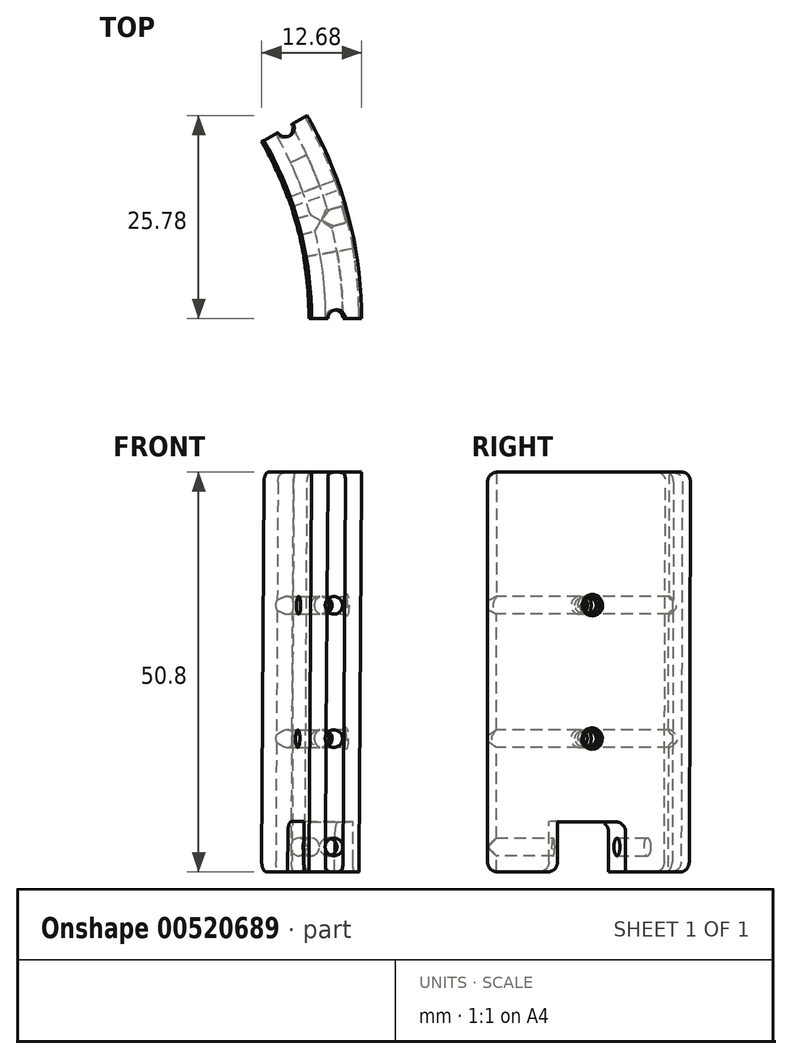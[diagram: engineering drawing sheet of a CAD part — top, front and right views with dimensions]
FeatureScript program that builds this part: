
annotation { "Feature Type Name" : "Feature", "Feature Type Description" : "" }
export const myFeature = defineFeature(function(context is Context, id is Id, definition is map)
    precondition{}
    {
        {
            var Q0;
            Q0=qCreatedBy(makeId("Front.planeOp"),FACE);
            var sketch = newSketch(context, id + "F0", { "sketchPlane" : qUnion([Q0])});
            skLineSegment(sketch, "E0", {"start": v(0, 0) * mm, "end": v(0, 50.8) * mm});
            skLineSegment(sketch, "E1", {"start": v(0, 50.8) * mm, "end": v(51.56, 50.8) * mm});
            skLineSegment(sketch, "E2", {"start": v(0, 0) * mm, "end": v(51.23, 0) * mm});
            skLineSegment(sketch, "E3", {"start": v(51.23, 0) * mm, "end": v(51.56, 50.8) * mm});
            skSolve(sketch);
        }
        {
            var Q0;
            Q0=makeQuery(id+"F0.imprint","IMPRINT",FACE,{"disambiguationData":[TD([[makeQuery(id+"F0.imprint","IMPRINT",EDGE,{"derivedFrom":sQuery(id+"F0.wireOp",EDGE,"E0")}),-1.0]])]});
            var Q1;
            Q1=sQuery(id+"F0.wireOp",EDGE,"E0");
            revolve(context, id + "F1", {"entities" : qUnion([Q0]), "axis" : qUnion([Q1]), "revolveType" : RevolveType.ONE_DIRECTION, "angle" : 30 * degree});
        }
        {
            var Q0;
            Q0=makeQuery(id+"F1.opRevolve","CAP_FACE",FACE,{"disambiguationData":[OSD([sQuery(id+"F0.wireOp",EDGE,"E0"),sQuery(id+"F0.wireOp",EDGE,"E1"),sQuery(id+"F0.wireOp",EDGE,"E2"),sQuery(id+"F0.wireOp",EDGE,"E3")])],"isStart":true});
            var sketch = newSketch(context, id + "F2", { "sketchPlane" : qUnion([Q0])});
            skLineSegment(sketch, "E4", {"start": v(0, 50.8) * mm, "end": v(0, 0) * mm});
            skLineSegment(sketch, "E5", {"start": v(0, 0) * mm, "end": v(44.88, 0) * mm});
            skLineSegment(sketch, "E6", {"start": v(0, 50.8) * mm, "end": v(45.21, 50.8) * mm});
            skLineSegment(sketch, "E7", {"start": v(45.21, 50.8) * mm, "end": v(44.88, 0) * mm});
            skSolve(sketch);
        }
        {
            var Q0;
            Q0=qSketchRegion(id+"F2",true);
            var Q1;
            Q1=sQuery(id+"F2.wireOp",EDGE,"E4");
            revolve(context, id + "F3", {"operationType" : NewBodyOperationType.REMOVE, "entities" : qUnion([Q0]), "axis" : qUnion([Q1]), "revolveType" : RevolveType.FULL, "oppositeDirection" : true});
        }
        {
            var Q0;
            Q0=makeQuery(id+"F1.opRevolve","CAP_FACE",FACE,{"disambiguationData":[OSD([sQuery(id+"F0.wireOp",EDGE,"E0"),sQuery(id+"F0.wireOp",EDGE,"E1"),sQuery(id+"F0.wireOp",EDGE,"E2"),sQuery(id+"F0.wireOp",EDGE,"E3")])],"isStart":true});
            var sketch = newSketch(context, id + "F4", { "sketchPlane" : qUnion([Q0])});
            skLineSegment(sketch, "E8", {"start": v(0, 0) * mm, "end": v(51.23, 0) * mm, "construction": true});
            skLineSegment(sketch, "E9", {"start": v(51.23, 0) * mm, "end": v(51.27, 6.35) * mm});
            skLineSegment(sketch, "E10", {"start": v(51.27, 6.35) * mm, "end": v(44.92, 6.4) * mm});
            skLineSegment(sketch, "E11", {"start": v(44.92, 6.4) * mm, "end": v(44.88, 0) * mm});
            skLineSegment(sketch, "E12", {"start": v(44.88, 0) * mm, "end": v(51.23, 0) * mm});
            skLineSegment(sketch, "E13", {"start": v(0, -1.63) * mm, "end": v(0, 22.61) * mm, "construction": true});
            skSolve(sketch);
        }
        {
            var Q0;
            Q0=qSketchRegion(id+"F4",true);
            var Q1;
            Q1=sQuery(id+"F4.wireOp",EDGE,"E13");
            revolve(context, id + "F5", {"operationType" : NewBodyOperationType.REMOVE, "entities" : qUnion([Q0]), "axis" : qUnion([Q1]), "revolveType" : RevolveType.ONE_DIRECTION, "angle" : 20 * degree});
        }
        {
            var Q0;
            Q0=qSketchRegion(id+"F4",true);
            var Q1;
            Q1=sQuery(id+"F4.wireOp",EDGE,"E13");
            revolve(context, id + "F6", {"operationType" : NewBodyOperationType.ADD, "entities" : qUnion([Q0]), "axis" : qUnion([Q1]), "revolveType" : RevolveType.ONE_DIRECTION, "angle" : 10 * degree});
        }
        {
            var Q0;
            Q0=makeQuery(id+"F6.boolean.opBoolean","MERGE",FACE,{"derivedFrom":[makeQuery(id+"F1.opRevolve","CAP_FACE",FACE,{"disambiguationData":[OSD([sQuery(id+"F0.wireOp",EDGE,"E0"),sQuery(id+"F0.wireOp",EDGE,"E1"),sQuery(id+"F0.wireOp",EDGE,"E2"),sQuery(id+"F0.wireOp",EDGE,"E3")])],"isStart":true}),makeQuery(id+"F6.opRevolve","CAP_FACE",FACE,{"disambiguationData":[OSD([sQuery(id+"F4.wireOp",EDGE,"E9"),sQuery(id+"F4.wireOp",EDGE,"E10"),sQuery(id+"F4.wireOp",EDGE,"E11"),sQuery(id+"F4.wireOp",EDGE,"E12")])],"isStart":true})]});
            var sketch = newSketch(context, id + "F7", { "sketchPlane" : qUnion([Q0])});
            skLineSegment(sketch, "E14", {"start": v(0, 0) * mm, "end": v(0, 25.16) * mm, "construction": true});
            skLineSegment(sketch, "E15", {"start": v(45.21, 50.8) * mm, "end": v(48.39, 50.8) * mm, "construction": true});
            skLineSegment(sketch, "E16", {"start": v(44.88, 0) * mm, "end": v(48.06, 0) * mm, "construction": true});
            skLineSegment(sketch, "E17", {"start": v(48.06, 0) * mm, "end": v(48.08, 4.3) * mm, "construction": true});
            skPoint(sketch, "E18", {"position": v(48.08, 3.17) * mm});
            skCircle(sketch, "E19", {"center": v(48.08, 3.17) * mm, "radius": 1.12 * mm, "construction": true});
            skLineSegment(sketch, "E20", {"start": v(0, 0) * mm, "end": v(48.06, 0) * mm, "construction": true});
            skLineSegment(sketch, "E21", {"start": v(48.06, 0) * mm, "end": v(48.06, 16.93) * mm, "construction": true});
            skLineSegment(sketch, "E22", {"start": v(48.06, 16.93) * mm, "end": v(48.06, 33.87) * mm, "construction": true});
            skCircle(sketch, "E23", {"center": v(48.06, 33.87) * mm, "radius": 1.12 * mm});
            skCircle(sketch, "E24", {"center": v(48.06, 16.93) * mm, "radius": 1.12 * mm});
            skSolve(sketch);
        }
        {
            var Q0;
            Q0=qSketchRegion(id+"F7",true);
            var Q1;
            Q1=sQuery(id+"F7.wireOp",EDGE,"E14");
            revolve(context, id + "F8", {"operationType" : NewBodyOperationType.REMOVE, "entities" : qUnion([Q0]), "axis" : qUnion([Q1]), "revolveType" : RevolveType.FULL, "oppositeDirection" : true});
        }
        {
            var Q0;
            Q0=makeQuery(id+"F6.opRevolve","SWEPT_FACE",FACE,{"disambiguationData":[OSD([sQuery(id+"F4.wireOp",EDGE,"E12")])]});
            var sketch = newSketch(context, id + "F9", { "sketchPlane" : qUnion([Q0])});
            skLineSegment(sketch, "E25", {"start": v(51.23, 0) * mm, "end": v(48.06, 0) * mm, "construction": true});
            skCircle(sketch, "E26", {"center": v(48.06, 0) * mm, "radius": 1.11 * mm});
            skSolve(sketch);
        }
        {
            var Q0;
            Q0=makeQuery(id+"F1.opRevolve","SWEPT_FACE",FACE,{"disambiguationData":[OSD([sQuery(id+"F0.wireOp",EDGE,"E1")])]});
            var sketch = newSketch(context, id + "F10", { "sketchPlane" : qUnion([Q0])});
            skLineSegment(sketch, "E27", {"start": v(51.56, 0) * mm, "end": v(48.39, 0) * mm, "construction": true});
            skCircle(sketch, "E28", {"center": v(48.39, 0) * mm, "radius": 1.11 * mm});
            skSolve(sketch);
        }
        {
            var Q0;
            Q0=makeQuery(id+"F1.opRevolve","SWEPT_FACE",FACE,{"disambiguationData":[OSD([sQuery(id+"F0.wireOp",EDGE,"E2")])]});
            var sketch = newSketch(context, id + "F11", { "sketchPlane" : qUnion([Q0])});
            skLineSegment(sketch, "E29", {"start": v(44.37, -25.62) * mm, "end": v(41.62, -24.03) * mm, "construction": true});
            skCircle(sketch, "E30", {"center": v(41.62, -24.03) * mm, "radius": 1.11 * mm});
            skSolve(sketch);
        }
        {
            var Q0;
            Q0=makeQuery(id+"F1.opRevolve","SWEPT_FACE",FACE,{"disambiguationData":[OSD([sQuery(id+"F0.wireOp",EDGE,"E1")])]});
            var sketch = newSketch(context, id + "F12", { "sketchPlane" : qUnion([Q0])});
            skLineSegment(sketch, "E31", {"start": v(44.65, 25.78) * mm, "end": v(41.9, 24.2) * mm, "construction": true});
            skCircle(sketch, "E32", {"center": v(41.9, 24.2) * mm, "radius": 1.11 * mm});
            skSolve(sketch);
        }
        {
            var Q0;
            Q0=makeQuery(id+"F5.boolean.opBoolean","COPY",EDGE,{"derivedFrom":makeQuery(id+"F5.opRevolve","CAP_EDGE",EDGE,{"disambiguationData":[OSD([sQuery(id+"F4.wireOp",EDGE,"E10")])],"isStart":false})});
            var Q1;
            Q1=makeQuery(id+"F5.boolean.opBoolean","COPY",EDGE,{"derivedFrom":makeQuery(id+"F5.opRevolve","CAP_EDGE",EDGE,{"disambiguationData":[OSD([sQuery(id+"F4.wireOp",EDGE,"E12")])],"isStart":false})});
            var Q2;
            Q2=makeQuery(id+"F6.opRevolve","CAP_EDGE",EDGE,{"disambiguationData":[OSD([sQuery(id+"F4.wireOp",EDGE,"E12")])],"isStart":false});
            var Q3;
            Q3=makeQuery(id+"F6.opRevolve","CAP_EDGE",EDGE,{"disambiguationData":[OSD([sQuery(id+"F4.wireOp",EDGE,"E10")])],"isStart":false});
            var Q4;
            Q4=makeQuery(id+"F1.opRevolve","CAP_EDGE",EDGE,{"disambiguationData":[OSD([sQuery(id+"F0.wireOp",EDGE,"E2")])],"isStart":false});
            var Q5;
            Q5=makeQuery(id+"F6.opRevolve","CAP_EDGE",EDGE,{"disambiguationData":[OSD([sQuery(id+"F4.wireOp",EDGE,"E12")])],"isStart":true});
            var Q6;
            Q6=makeQuery(id+"F1.opRevolve","CAP_EDGE",EDGE,{"disambiguationData":[OSD([sQuery(id+"F0.wireOp",EDGE,"E1")])],"isStart":true});
            var Q7;
            Q7=makeQuery(id+"F1.opRevolve","CAP_EDGE",EDGE,{"disambiguationData":[OSD([sQuery(id+"F0.wireOp",EDGE,"E1")])],"isStart":false});
            fillet(context, id + "F13", {"entities" : qUnion([Q0, Q1, Q2, Q3, Q4, Q5, Q6, Q7]), "radius" : 1.27 * mm, "tangentPropagation" : true, "allowEdgeOverflow" : false});
        }
        {
            var Q0;
            Q0=qCreatedBy(makeId("Front.planeOp"),FACE);
            var sketch = newSketch(context, id + "F14", { "sketchPlane" : qUnion([Q0])});
            skLineSegment(sketch, "E33", {"start": v(0, 0) * mm, "end": v(48.06, 0) * mm, "construction": true});
            skLineSegment(sketch, "E34", {"start": v(48.06, 0) * mm, "end": v(48.06, 3.18) * mm, "construction": true});
            skCircle(sketch, "E35", {"center": v(48.06, 3.18) * mm, "radius": 1.12 * mm});
            skSolve(sketch);
        }
        {
            var Q0;
            Q0=qSketchRegion(id+"F14",true);
            var Q1;
            Q1=sQuery(id+"F7.wireOp",EDGE,"E14");
            revolve(context, id + "F15", {"operationType" : NewBodyOperationType.REMOVE, "entities" : qUnion([Q0]), "axis" : qUnion([Q1]), "revolveType" : RevolveType.ONE_DIRECTION, "angle" : 25 * degree});
        }
        {
            var Q1;
            {var subQ0=sQuery(id+"F10.wireOp",EDGE,"E28");var subQ1=makeQuery(id+"F1.opRevolve","CAP_EDGE",EDGE,{"disambiguationData":[OSD([sQuery(id+"F0.wireOp",EDGE,"E1")])],"isStart":true});var subQ2=makeQuery(id+"F10.imprint","INTERSECT",VERTEX,{"disambiguationData":[OD(0.0)],"derivedFrom":[subQ1,subQ0]});Q1=makeQuery(id+"F10.imprint","IMPRINT",FACE,{"disambiguationData":[TD([[makeQuery(id+"F10.imprint","IMPRINT",EDGE,{"disambiguationData":[TD([[subQ2,-1.0]])],"derivedFrom":subQ0}),1.0]])]});}
            var Q2;
            {var subQ0=sQuery(id+"F9.wireOp",EDGE,"E26");var subQ1=makeQuery(id+"F6.opRevolve","CAP_EDGE",EDGE,{"disambiguationData":[OSD([sQuery(id+"F4.wireOp",EDGE,"E12")])],"isStart":true});var subQ2=makeQuery(id+"F9.imprint","INTERSECT",VERTEX,{"disambiguationData":[OD(0.0)],"derivedFrom":[subQ1,subQ0]});Q2=makeQuery(id+"F9.imprint","IMPRINT",FACE,{"disambiguationData":[TD([[makeQuery(id+"F9.imprint","IMPRINT",EDGE,{"disambiguationData":[TD([[subQ2,1.0]])],"derivedFrom":subQ0}),1.0]])]});}
            loft(context, id + "F16", {"operationType" : NewBodyOperationType.REMOVE, "sheetProfilesArray" : [{ "sheetProfileEntities" : qUnion([Q1]) }, { "sheetProfileEntities" : qUnion([Q2]) }]});
        }
        {
            var Q1;
            {var subQ0=sQuery(id+"F12.wireOp",EDGE,"E32");var subQ1=makeQuery(id+"F1.opRevolve","CAP_EDGE",EDGE,{"disambiguationData":[OSD([sQuery(id+"F0.wireOp",EDGE,"E1")])],"isStart":false});var subQ2=makeQuery(id+"F12.imprint","INTERSECT",VERTEX,{"disambiguationData":[OD(0.0)],"derivedFrom":[subQ1,subQ0]});Q1=makeQuery(id+"F12.imprint","IMPRINT",FACE,{"disambiguationData":[TD([[makeQuery(id+"F12.imprint","IMPRINT",EDGE,{"disambiguationData":[TD([[subQ2,1.0]])],"derivedFrom":subQ0}),1.0]])]});}
            var Q2;
            {var subQ0=sQuery(id+"F11.wireOp",EDGE,"E30");var subQ1=makeQuery(id+"F1.opRevolve","CAP_EDGE",EDGE,{"disambiguationData":[OSD([sQuery(id+"F0.wireOp",EDGE,"E2")])],"isStart":false});var subQ2=makeQuery(id+"F11.imprint","INTERSECT",VERTEX,{"disambiguationData":[OD(0.0)],"derivedFrom":[subQ1,subQ0]});Q2=makeQuery(id+"F11.imprint","IMPRINT",FACE,{"disambiguationData":[TD([[makeQuery(id+"F11.imprint","IMPRINT",EDGE,{"disambiguationData":[TD([[subQ2,-1.0]])],"derivedFrom":subQ0}),1.0]])]});}
            loft(context, id + "F17", {"operationType" : NewBodyOperationType.REMOVE, "sheetProfilesArray" : [{ "sheetProfileEntities" : qUnion([Q1]) }, { "sheetProfileEntities" : qUnion([Q2]) }]});
        }
        {
            var Q0;
            Q0=qCreatedBy(makeId("Right.planeOp"),FACE);
            var sketch = newSketch(context, id + "F18", { "sketchPlane" : qUnion([Q0])});
            skLineSegment(sketch, "E36", {"start": v(0, 0) * mm, "end": v(0, 16.93) * mm, "construction": true});
            skLineSegment(sketch, "E37", {"start": v(0, 16.93) * mm, "end": v(0, 33.87) * mm, "construction": true});
            skCircle(sketch, "E38", {"center": v(0, 16.93) * mm, "radius": 1.11 * mm});
            skCircle(sketch, "E39", {"center": v(0, 33.87) * mm, "radius": 1.11 * mm});
            skSolve(sketch);
        }
        {
            var Q0;
            Q0=qCreatedBy(makeId("Top.planeOp"),FACE);
            cPlane(context, id + "F19", {"entities" : qUnion([Q0]), "cplaneType" : CPlaneType.OFFSET, "offset" : 16.93 * mm, "width" : 152.4 * mm, "height" : 152.4 * mm});
        }
        {
            var Q0;
            Q0=qCreatedBy(id+"F19.planeOp",FACE);
            var sketch = newSketch(context, id + "F20", { "sketchPlane" : qUnion([Q0])});
            skLineSegment(sketch, "E40", {"start": v(0, 0) * mm, "end": v(50.8, 0) * mm, "construction": true});
            skLineSegment(sketch, "E41", {"start": v(50.8, 0) * mm, "end": v(0.77, 0) * mm, "construction": true});
            skLineSegment(sketch, "E42", {"start": v(0.77, 0) * mm, "end": v(67.27, 17.82) * mm});
            skSolve(sketch);
        }
        {
            var Q0;
            Q0 = qSketchRegion(id + "F18", true);
            var Q1;
            Q1 = qConstructionFilter(qBodyType(qCreatedBy(id + "F18" ,EDGE), BodyType.WIRE), ConstructionObject.NO);
            var Q2;
            Q2 = qConstructionFilter(qBodyType(qCreatedBy(id + "F20" ,EDGE), BodyType.WIRE), ConstructionObject.NO);
            sweep(context, id + "F21", {"operationType" : NewBodyOperationType.REMOVE, "profiles" : qUnion([Q0]), "surfaceProfiles" : qUnion([Q1]), "path" : qUnion([Q2])});
        }
        {
            var Q0;
            Q0=makeQuery(id+"F21.boolean.opBoolean","INTERSECT",EDGE,{"derivedFrom":[makeQuery(id+"F6.boolean.opBoolean","MERGE",FACE,{"derivedFrom":[makeQuery(id+"F1.opRevolve","SWEPT_FACE",FACE,{"disambiguationData":[OSD([sQuery(id+"F0.wireOp",EDGE,"E3")])]}),makeQuery(id+"F6.opRevolve","SWEPT_FACE",FACE,{"disambiguationData":[OSD([sQuery(id+"F4.wireOp",EDGE,"E9")])]})]}),makeQuery(id+"F21.opSweep","SWEPT_FACE",FACE,{"disambiguationData":[OSD([sQuery(id+"F18.wireOp",EDGE,"E39"),sQuery(id+"F20.wireOp",EDGE,"E42")])]})]});
            var Q1;
            Q1=makeQuery(id+"F21.boolean.opBoolean","INTERSECT",EDGE,{"disambiguationData":[OD(0.0)],"derivedFrom":[makeQuery(id+"F8.boolean.opBoolean","COPY",FACE,{"derivedFrom":makeQuery(id+"F8.opRevolve","SWEPT_FACE",FACE,{"disambiguationData":[OSD([sQuery(id+"F7.wireOp",EDGE,"E23")])]})}),makeQuery(id+"F21.opSweep","SWEPT_FACE",FACE,{"disambiguationData":[OSD([sQuery(id+"F18.wireOp",EDGE,"E39"),sQuery(id+"F20.wireOp",EDGE,"E42")])]})]});
            var Q2;
            Q2=makeQuery(id+"F21.boolean.opBoolean","INTERSECT",EDGE,{"disambiguationData":[OD(0.0)],"derivedFrom":[makeQuery(id+"F8.boolean.opBoolean","COPY",FACE,{"derivedFrom":makeQuery(id+"F8.opRevolve","SWEPT_FACE",FACE,{"disambiguationData":[OSD([sQuery(id+"F7.wireOp",EDGE,"E24")])]})}),makeQuery(id+"F21.opSweep","SWEPT_FACE",FACE,{"disambiguationData":[OSD([sQuery(id+"F18.wireOp",EDGE,"E38"),sQuery(id+"F20.wireOp",EDGE,"E42")])]})]});
            var Q3;
            Q3=makeQuery(id+"F21.boolean.opBoolean","INTERSECT",EDGE,{"derivedFrom":[makeQuery(id+"F6.boolean.opBoolean","MERGE",FACE,{"derivedFrom":[makeQuery(id+"F1.opRevolve","SWEPT_FACE",FACE,{"disambiguationData":[OSD([sQuery(id+"F0.wireOp",EDGE,"E3")])]}),makeQuery(id+"F6.opRevolve","SWEPT_FACE",FACE,{"disambiguationData":[OSD([sQuery(id+"F4.wireOp",EDGE,"E9")])]})]}),makeQuery(id+"F21.opSweep","SWEPT_FACE",FACE,{"disambiguationData":[OSD([sQuery(id+"F18.wireOp",EDGE,"E38"),sQuery(id+"F20.wireOp",EDGE,"E42")])]})]});
            fillet(context, id + "F22", {"entities" : qUnion([Q0, Q1, Q2, Q3]), "radius" : 0.25 * mm, "tangentPropagation" : true, "allowEdgeOverflow" : false});
        }
    });
